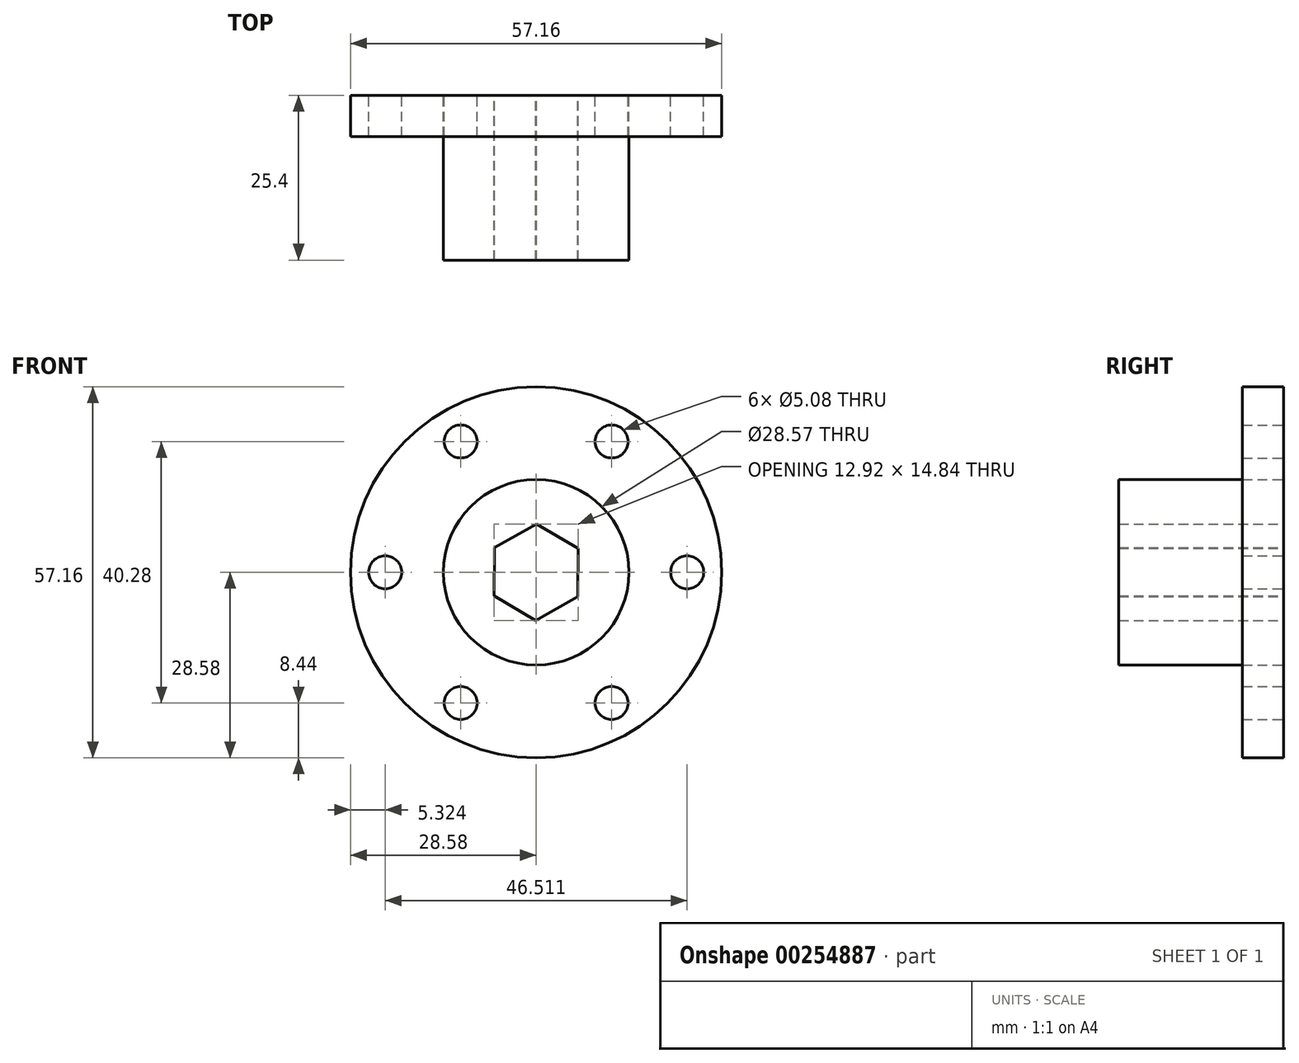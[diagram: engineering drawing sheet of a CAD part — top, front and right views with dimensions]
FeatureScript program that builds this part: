
annotation { "Feature Type Name" : "Feature", "Feature Type Description" : "" }
export const myFeature = defineFeature(function(context is Context, id is Id, definition is map)
    precondition{}
    {
        {
            var Q0;
            Q0=qCreatedBy(makeId("Front.planeOp"),FACE);
            var sketch = newSketch(context, id + "F0", { "sketchPlane" : qUnion([Q0])});
            skCircle(sketch, "E0", {"center": v(0, 0) * mm, "radius": 28.58 * mm});
            skCircle(sketch, "E1.cCircle", {"center": v(0, 0) * mm, "radius": 20.14 * mm, "construction": true});
            skPoint(sketch, "E1.0.midPoint", {"position": v(0, 20.14) * mm});
            skCircle(sketch, "E2", {"center": v(-11.63, 20.14) * mm, "radius": 2.54 * mm});
            skCircle(sketch, "E3", {"center": v(11.63, 20.14) * mm, "radius": 2.54 * mm});
            skCircle(sketch, "E4", {"center": v(23.26, 0) * mm, "radius": 2.54 * mm});
            skCircle(sketch, "E5", {"center": v(11.63, -20.14) * mm, "radius": 2.54 * mm});
            skCircle(sketch, "E6", {"center": v(-11.63, -20.14) * mm, "radius": 2.54 * mm});
            skCircle(sketch, "E7", {"center": v(-23.26, 0) * mm, "radius": 2.54 * mm});
            skCircle(sketch, "E8.cCircle", {"center": v(0, 0) * mm, "radius": 6.43 * mm, "construction": true});
            skLineSegment(sketch, "E8.0", {"start": v(-6.4, 3.77) * mm, "end": v(0.07, 7.42) * mm});
            skLineSegment(sketch, "E8.1", {"start": v(0.07, 7.42) * mm, "end": v(6.46, 3.65) * mm});
            skLineSegment(sketch, "E8.2", {"start": v(6.46, 3.65) * mm, "end": v(6.4, -3.77) * mm});
            skLineSegment(sketch, "E8.3", {"start": v(6.4, -3.77) * mm, "end": v(-0.07, -7.42) * mm});
            skLineSegment(sketch, "E8.4", {"start": v(-0.07, -7.42) * mm, "end": v(-6.46, -3.65) * mm});
            skLineSegment(sketch, "E8.5", {"start": v(-6.46, -3.65) * mm, "end": v(-6.4, 3.77) * mm});
            skPoint(sketch, "E8.0.midPoint", {"position": v(-3.16, 5.6) * mm});
            skCircle(sketch, "E9", {"center": v(0, 0) * mm, "radius": 14.29 * mm});
            skSolve(sketch);
        }
        {
            var Q0;
            Q0=makeQuery(id+"F0.imprint","IMPRINT",FACE,{"disambiguationData":[TD([[makeQuery(id+"F0.imprint","IMPRINT",EDGE,{"derivedFrom":sQuery(id+"F0.wireOp",EDGE,"E8.0")}),1.0]])]});
            extrude(context, id + "F1", {"entities" : qUnion([Q0]), "depth" : 25.4 * mm});
        }
        {
            var Q0;
            Q0=makeQuery(id+"F0.imprint","IMPRINT",FACE,{"disambiguationData":[TD([[makeQuery(id+"F0.imprint","IMPRINT",EDGE,{"derivedFrom":sQuery(id+"F0.wireOp",EDGE,"E0")}),1.0]])]});
            extrude(context, id + "F2", {"entities" : qUnion([Q0]), "depth" : 6.35 * mm});
        }
        {
            var Q0;
            Q0=sQuery(id+"F0.wireOp",EDGE,"E9");
            extrude(context, id + "F3", {"bodyType" : ToolBodyType.SURFACE, "surfaceEntities" : qUnion([Q0]), "depth" : 8.9 * mm, "hasSecondDirection" : true, "secondDirectionOppositeDirection" : true, "secondDirectionDepth" : 0.89 * mm});
        }
    });
